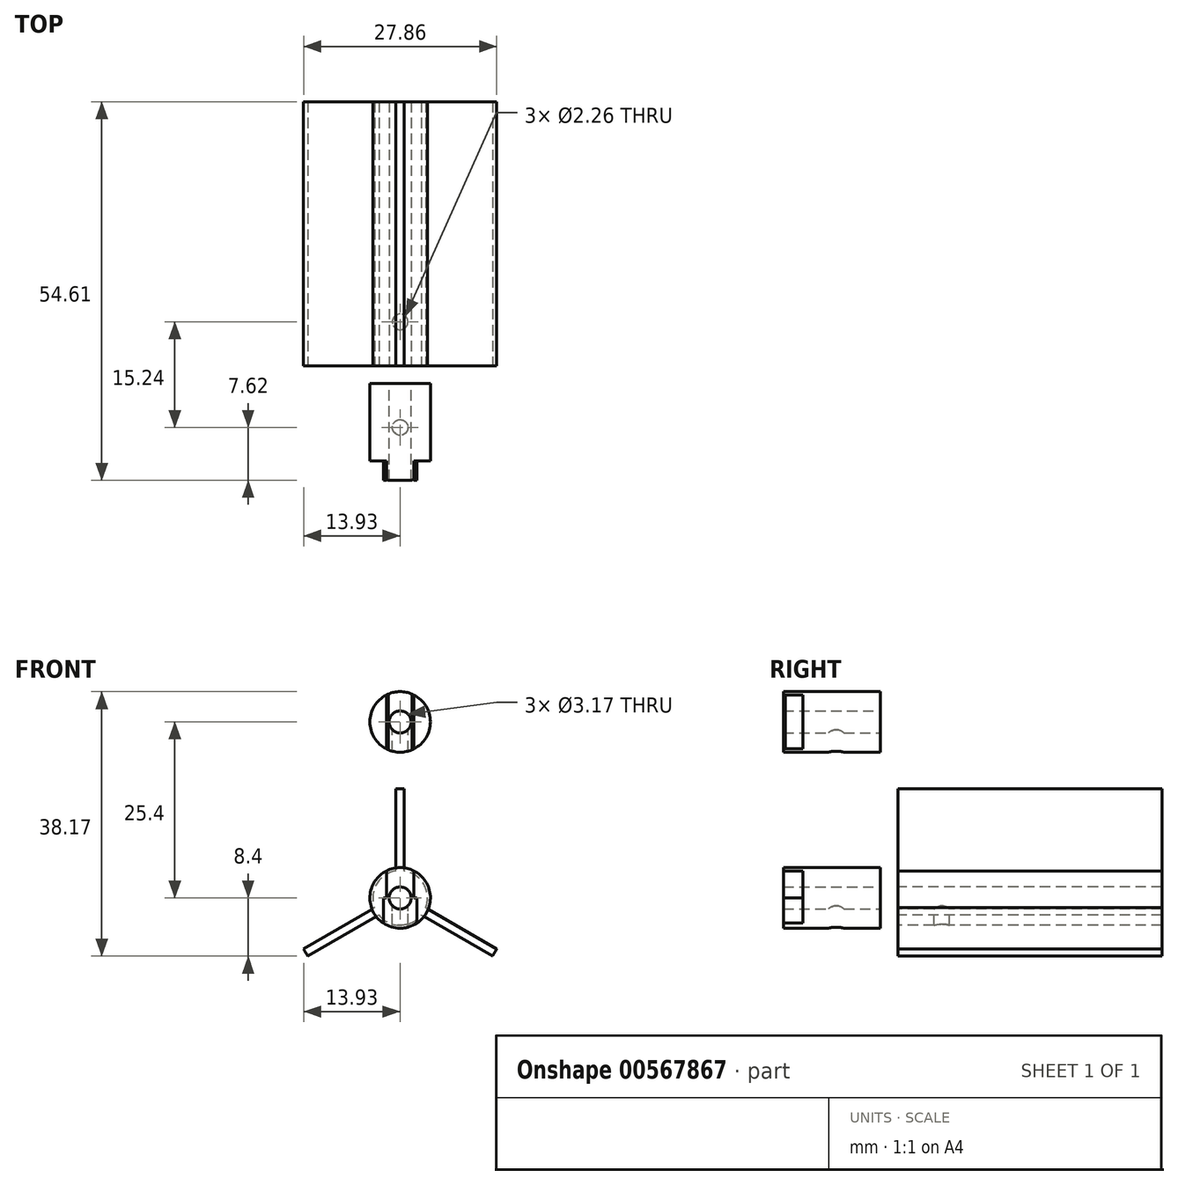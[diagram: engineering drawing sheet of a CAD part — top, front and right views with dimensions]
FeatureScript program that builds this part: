
annotation { "Feature Type Name" : "Feature", "Feature Type Description" : "" }
export const myFeature = defineFeature(function(context is Context, id is Id, definition is map)
    precondition{}
    {
        {
            var Q0;
            Q0=qCreatedBy(makeId("Front.planeOp"),FACE);
            var sketch = newSketch(context, id + "F0", { "sketchPlane" : qUnion([Q0])});
            skCircle(sketch, "E0", {"center": v(0, 0) * mm, "radius": 15.75 * mm});
            skCircle(sketch, "E1", {"center": v(0, 0) * mm, "radius": 1.59 * mm});
            skSolve(sketch);
        }
        {
            var Q0;
            Q0=makeQuery(id+"F0.imprint","IMPRINT",FACE,{"disambiguationData":[TD([[makeQuery(id+"F0.imprint","IMPRINT",EDGE,{"derivedFrom":sQuery(id+"F0.wireOp",EDGE,"E0")}),1.0]])]});
            extrude(context, id + "F1", {"entities" : qUnion([Q0]), "oppositeDirection" : true, "depth" : 38.1 * mm, "offsetDistance" : 25.4 * mm});
        }
        {
            var Q0;
            Q0=qCreatedBy(makeId("Front.planeOp"),FACE);
            cPlane(context, id + "F2", {"entities" : qUnion([Q0]), "cplaneType" : CPlaneType.OFFSET, "offset" : 2.54 * mm, "width" : 152.4 * mm, "height" : 152.4 * mm});
        }
        {
            var Q0;
            Q0=qCreatedBy(id+"F2.planeOp",FACE);
            var sketch = newSketch(context, id + "F3", { "sketchPlane" : qUnion([Q0])});
            skLineSegment(sketch, "E2", {"start": v(0, 3.94) * mm, "end": v(0, 18.23) * mm, "construction": true});
            skLineSegment(sketch, "E3", {"start": v(-3.4, -1.97) * mm, "end": v(-15.8, -9.12) * mm, "construction": true});
            skLineSegment(sketch, "E4", {"start": v(3.4, -1.97) * mm, "end": v(15.8, -9.12) * mm, "construction": true});
            skArc(sketch, "E5", {"start": v(-0.6, 3.89) * mm, "mid": v(-3.4, 1.97) * mm, "end": v(-3.67, -1.42) * mm});
            skLineSegment(sketch, "E6.0", {"start": v(0.6, 3.89) * mm, "end": v(0.6, 18.22) * mm});
            skLineSegment(sketch, "E7.0", {"start": v(-0.6, 3.89) * mm, "end": v(-0.6, 18.22) * mm});
            skLineSegment(sketch, "E8.0", {"start": v(3.67, -1.42) * mm, "end": v(16.09, -8.58) * mm});
            skLineSegment(sketch, "E9.0", {"start": v(3.06, -2.47) * mm, "end": v(15.48, -9.64) * mm});
            skLineSegment(sketch, "E10.0", {"start": v(-3.67, -1.42) * mm, "end": v(-16.09, -8.58) * mm});
            skLineSegment(sketch, "E11.0", {"start": v(-3.06, -2.47) * mm, "end": v(-15.48, -9.64) * mm});
            skArc(sketch, "E12", {"start": v(-0.6, 18.22) * mm, "mid": v(-15.8, 9.12) * mm, "end": v(-16.09, -8.58) * mm});
            skArc(sketch, "E13.trimOffspring", {"start": v(3.67, -1.42) * mm, "mid": v(3.4, 1.97) * mm, "end": v(0.6, 3.89) * mm});
            skArc(sketch, "E14.trimOffspring", {"start": v(-3.06, -2.47) * mm, "mid": v(0, -3.94) * mm, "end": v(3.06, -2.47) * mm});
            skArc(sketch, "E15.trimOffspring", {"start": v(16.09, -8.58) * mm, "mid": v(15.8, 9.12) * mm, "end": v(0.6, 18.22) * mm});
            skArc(sketch, "E16.trimOffspring", {"start": v(-15.48, -9.64) * mm, "mid": v(0, -18.23) * mm, "end": v(15.48, -9.64) * mm});
            skSolve(sketch);
        }
        {
            var Q0;
            Q0=makeQuery(id+"F3.imprint","IMPRINT",FACE,{"disambiguationData":[TD([[makeQuery(id+"F3.imprint","IMPRINT",EDGE,{"derivedFrom":sQuery(id+"F3.wireOp",EDGE,"E5")}),-1.0]])]});
            var Q1;
            Q1=makeQuery(id+"F3.imprint","IMPRINT",FACE,{"disambiguationData":[TD([[makeQuery(id+"F3.imprint","IMPRINT",EDGE,{"derivedFrom":sQuery(id+"F3.wireOp",EDGE,"E6.0")}),-1.0]])]});
            var Q2;
            Q2=makeQuery(id+"F3.imprint","IMPRINT",FACE,{"disambiguationData":[TD([[makeQuery(id+"F3.imprint","IMPRINT",EDGE,{"derivedFrom":sQuery(id+"F3.wireOp",EDGE,"E9.0")}),-1.0]])]});
            extrude(context, id + "F4", {"entities" : qUnion([Q0, Q1, Q2]), "operationType" : NewBodyOperationType.REMOVE, "endBound" : BoundingType.THROUGH_ALL, "oppositeDirection" : true, "depth" : 25.4 * mm, "offsetDistance" : 25.4 * mm});
        }
        {
            var Q0;
            Q0=qCreatedBy(makeId("Top.planeOp"),FACE);
            var sketch = newSketch(context, id + "F5", { "sketchPlane" : qUnion([Q0])});
            skPoint(sketch, "E17", {"position": v(0, 6.35) * mm});
            skSolve(sketch);
        }
        {
            var Q0;
            Q0=sQuery(id+"F5.wireOp",VERTEX,"E17");
            var Q1;
            Q1=makeQuery(id+"F1.opExtrude","SWEPT_BODY",BODY,{"disambiguationData":[OSD([sQuery(id+"F0.wireOp",EDGE,"E0"),sQuery(id+"F0.wireOp",EDGE,"E1")])]});
            hole(context, id + "F6", {"style" : HoleStyle.SIMPLE, "endStyle" : HoleEndStyle.THROUGH, "holeDiameter" : 2.26 * mm, "isTappedThrough" : true, "tappedDepth" : 12.7 * mm, "tapClearance" : 3, "startFromSketch" : true, "locations" : qUnion([Q0]), "scope" : qUnion([Q1])});
        }
        {
            var Q0;
            Q0=qCreatedBy(id+"F2.planeOp",FACE);
            var sketch = newSketch(context, id + "F7", { "sketchPlane" : qUnion([Q0])});
            skCircle(sketch, "E18", {"center": v(0, 0) * mm, "radius": 4.37 * mm});
            skCircle(sketch, "E19", {"center": v(0, 0) * mm, "radius": 1.59 * mm});
            skSolve(sketch);
        }
        {
            var Q0;
            Q0=makeQuery(id+"F7.imprint","IMPRINT",FACE,{"disambiguationData":[TD([[makeQuery(id+"F7.imprint","IMPRINT",EDGE,{"derivedFrom":sQuery(id+"F7.wireOp",EDGE,"E18")}),1.0]])]});
            extrude(context, id + "F8", {"entities" : qUnion([Q0]), "depth" : 13.97 * mm, "offsetDistance" : 25.4 * mm});
        }
        {
            var Q0;
            Q0=makeQuery(id+"F8.opExtrude","CAP_FACE",FACE,{"disambiguationData":[OSD([sQuery(id+"F7.wireOp",EDGE,"E18")])],"isStart":false});
            cPlane(context, id + "F9", {"entities" : qUnion([Q0]), "cplaneType" : CPlaneType.OFFSET, "offset" : 2.54 * mm, "width" : 152.4 * mm, "height" : 152.4 * mm});
        }
        {
            var Q0;
            Q0=qCreatedBy(id+"F9.planeOp",FACE);
            var sketch = newSketch(context, id + "F10", { "sketchPlane" : qUnion([Q0])});
            skLineSegment(sketch, "E20", {"start": v(-2.41, 11.08) * mm, "end": v(-2.41, -12.93) * mm});
            skLineSegment(sketch, "E21", {"start": v(-2.41, -12.93) * mm, "end": v(-9.87, -12.93) * mm});
            skLineSegment(sketch, "E22", {"start": v(-9.87, -12.93) * mm, "end": v(-9.87, 11.08) * mm});
            skLineSegment(sketch, "E23", {"start": v(-9.87, 11.08) * mm, "end": v(-2.41, 11.08) * mm});
            skLineSegment(sketch, "E24.MirrorCS", {"start": v(9.87, 11.08) * mm, "end": v(2.41, 11.08) * mm});
            skLineSegment(sketch, "E25.MirrorCS", {"start": v(9.87, -12.93) * mm, "end": v(9.87, 11.08) * mm});
            skLineSegment(sketch, "E26.MirrorCS", {"start": v(2.41, 11.08) * mm, "end": v(2.41, -12.93) * mm});
            skLineSegment(sketch, "E27.MirrorCS", {"start": v(2.41, -12.93) * mm, "end": v(9.87, -12.93) * mm});
            skSolve(sketch);
        }
        {
            var Q0;
            Q0=makeQuery(id+"F10.imprint","IMPRINT",FACE,{"disambiguationData":[TD([[makeQuery(id+"F10.imprint","IMPRINT",EDGE,{"derivedFrom":sQuery(id+"F10.wireOp",EDGE,"E20")}),-1.0]])]});
            var Q1;
            Q1=makeQuery(id+"F10.imprint","IMPRINT",FACE,{"disambiguationData":[TD([[makeQuery(id+"F10.imprint","IMPRINT",EDGE,{"derivedFrom":sQuery(id+"F10.wireOp",EDGE,"E24.MirrorCS")}),1.0]])]});
            extrude(context, id + "F11", {"entities" : qUnion([Q0, Q1]), "operationType" : NewBodyOperationType.REMOVE, "oppositeDirection" : true, "depth" : 5.33 * mm, "offsetDistance" : 25.4 * mm});
        }
        {
            var Q0;
            Q0=qCreatedBy(makeId("Top.planeOp"),FACE);
            var sketch = newSketch(context, id + "F12", { "sketchPlane" : qUnion([Q0])});
            skPoint(sketch, "E28", {"position": v(0, -8.9) * mm});
            skSolve(sketch);
        }
        {
            var Q0;
            Q0=sQuery(id+"F12.wireOp",VERTEX,"E28");
            var Q1;
            Q1=makeQuery(id+"F8.opExtrude","SWEPT_BODY",BODY,{"disambiguationData":[OSD([sQuery(id+"F7.wireOp",EDGE,"E18"),sQuery(id+"F7.wireOp",EDGE,"E19")])]});
            hole(context, id + "F13", {"style" : HoleStyle.SIMPLE, "endStyle" : HoleEndStyle.THROUGH, "holeDiameter" : 2.26 * mm, "isTappedThrough" : true, "tappedDepth" : 12.7 * mm, "tapClearance" : 3, "startFromSketch" : true, "locations" : qUnion([Q0]), "scope" : qUnion([Q1])});
        }
        {
            var Q0;
            Q0=makeQuery(id+"F8.opExtrude","SWEPT_BODY",BODY,{"disambiguationData":[OSD([sQuery(id+"F7.wireOp",EDGE,"E18"),sQuery(id+"F7.wireOp",EDGE,"E19")])]});
            var Q1;
            Q1=qCreatedBy(makeId("Top.planeOp"),FACE);
            transform(context, id + "F14", {"entities" : qUnion([Q0]), "transformType" : TransformType.TRANSLATION_DISTANCE, "transformDirection" : qUnion([Q1]), "distance" : 25.4 * mm, "makeCopy" : true});
        }
        {
            var Q0;
            Q0=qCreatedBy(makeId("Top.planeOp"),FACE);
            var sketch = newSketch(context, id + "F15", { "sketchPlane" : qUnion([Q0])});
            skLineSegment(sketch, "E29", {"start": v(-6.08, -13.72) * mm, "end": v(-1.98, -13.72) * mm});
            skLineSegment(sketch, "E30", {"start": v(-1.98, -13.72) * mm, "end": v(-1.98, -20.36) * mm});
            skLineSegment(sketch, "E31", {"start": v(-1.98, -20.36) * mm, "end": v(-6.08, -20.36) * mm});
            skLineSegment(sketch, "E32", {"start": v(-6.08, -20.36) * mm, "end": v(-6.08, -13.72) * mm});
            skLineSegment(sketch, "E33.MirrorCS", {"start": v(1.98, -20.36) * mm, "end": v(6.08, -20.36) * mm});
            skLineSegment(sketch, "E34.MirrorCS", {"start": v(1.98, -13.72) * mm, "end": v(1.98, -20.36) * mm});
            skLineSegment(sketch, "E35.MirrorCS", {"start": v(6.08, -13.72) * mm, "end": v(1.98, -13.72) * mm});
            skLineSegment(sketch, "E36.MirrorCS", {"start": v(6.08, -20.36) * mm, "end": v(6.08, -13.72) * mm});
            skSolve(sketch);
        }
        {
            var Q0;
            Q0=makeQuery(id+"F15.imprint","IMPRINT",FACE,{"disambiguationData":[TD([[makeQuery(id+"F15.imprint","IMPRINT",EDGE,{"derivedFrom":sQuery(id+"F15.wireOp",EDGE,"E29")}),-1.0]])]});
            var Q1;
            Q1=makeQuery(id+"F15.imprint","IMPRINT",FACE,{"disambiguationData":[TD([[makeQuery(id+"F15.imprint","IMPRINT",EDGE,{"derivedFrom":sQuery(id+"F15.wireOp",EDGE,"E33.MirrorCS")}),1.0]])]});
            extrude(context, id + "F16", {"entities" : qUnion([Q0, Q1]), "operationType" : NewBodyOperationType.REMOVE, "depth" : 38.1 * mm, "offsetDistance" : 25.4 * mm});
        }
        {
            var Q0;
            Q0=makeQuery(id+"F16.boolean.opBoolean","INTERSECT",EDGE,{"derivedFrom":[makeQuery(id+"F14.opPattern","COPY",FACE,{"derivedFrom":makeQuery(id+"F8.opExtrude","CAP_FACE",FACE,{"disambiguationData":[OSD([sQuery(id+"F7.wireOp",EDGE,"E18"),sQuery(id+"F7.wireOp",EDGE,"E19")])],"isStart":false}),"instanceName":"1"}),makeQuery(id+"F16.opExtrude","SWEPT_FACE",FACE,{"disambiguationData":[OSD([sQuery(id+"F15.wireOp",EDGE,"E30")])]})]});
            var Q1;
            Q1=makeQuery(id+"F16.boolean.opBoolean","INTERSECT",EDGE,{"derivedFrom":[makeQuery(id+"F14.opPattern","COPY",FACE,{"derivedFrom":makeQuery(id+"F8.opExtrude","CAP_FACE",FACE,{"disambiguationData":[OSD([sQuery(id+"F7.wireOp",EDGE,"E18"),sQuery(id+"F7.wireOp",EDGE,"E19")])],"isStart":false}),"instanceName":"1"}),makeQuery(id+"F16.opExtrude","SWEPT_FACE",FACE,{"disambiguationData":[OSD([sQuery(id+"F15.wireOp",EDGE,"E34.MirrorCS")])]})]});
            chamfer(context, id + "F17", {"entities" : qUnion([Q0, Q1]), "width" : 0.25 * mm, "tangentPropagation" : true});
        }
    });
